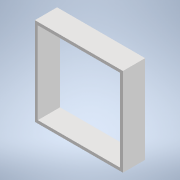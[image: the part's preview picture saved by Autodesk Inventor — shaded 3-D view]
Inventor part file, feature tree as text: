
AUTODESK INVENTOR PART (.ipt)
format: ipt  version: 2021.2 (Build 252289000, 289)  size: 163,840 bytes
history: native  units: mm
features: other x4, extrude x4, sketch x4, reference x1
ambient origin geometry x8: Origin, YZ Plane, XZ Plane, XY Plane, X Axis, Y Axis, Z Axis, Center Point
bodies: Body1 (feature_tree)
feature tree (13):
  other  "Твердое тело1"
  extrude  "Выдавливание1"  Depth=2.0mm
  extrude  "Выдавливание2"  Depth=10.0mm TaperAngle=0.0deg
  extrude  "Выдавливание3"  Depth=1.5mm TaperAngle=0.0deg
  extrude  "Выдавливание4"  Depth=4.0mm
  sketch  "Эскиз1"
  reference  "Ссылка1"
  sketch  "Эскиз2"
  sketch  "Эскиз3"
  sketch  "Эскиз4"
  parser-record x1  (decoder bookkeeping rows leaked as tree rows — omitted from the tree; the rows remain in map.json)
  other  "Сборка1.iam"
  other  "Середина 2:1"
note: 1 file-system path scrubbed to <path> (originals preserved in map.json)
